annotation { "Feature Type Name" : "Feature", "Feature Type Description" : "" }
export const myFeature = defineFeature(function(context is Context, id is Id, definition is map)
    precondition{}
    {
        {
            var Q0;
            Q0=qCreatedBy(makeId("Top.planeOp"),FACE);
            var sketch = newSketch(context, id + "F0", { "sketchPlane" : qUnion([Q0])});
            skLineSegment(sketch, "E0.bottom", {"start": v(-30.42, 27.45) * mm, "end": v(21.08, 27.45) * mm});
            skLineSegment(sketch, "E0.top", {"start": v(-30.42, -12.55) * mm, "end": v(21.08, -12.55) * mm});
            skLineSegment(sketch, "E0.left", {"start": v(-30.42, 27.45) * mm, "end": v(-30.42, -12.55) * mm});
            skLineSegment(sketch, "E0.right", {"start": v(21.08, 27.45) * mm, "end": v(21.08, -12.55) * mm});
            skLineSegment(sketch, "E1.bottom", {"start": v(-33.42, -15.55) * mm, "end": v(24.08, -15.55) * mm});
            skLineSegment(sketch, "E1.top", {"start": v(-33.42, 30.45) * mm, "end": v(24.08, 30.45) * mm});
            skLineSegment(sketch, "E1.left", {"start": v(-33.42, -15.55) * mm, "end": v(-33.42, 30.45) * mm});
            skLineSegment(sketch, "E1.right", {"start": v(24.08, -15.55) * mm, "end": v(24.08, 30.45) * mm});
            skLineSegment(sketch, "E2.bottom", {"start": v(94.89, 38.7) * mm, "end": v(41.39, 38.7) * mm});
            skLineSegment(sketch, "E2.top", {"start": v(94.89, -4.3) * mm, "end": v(41.39, -4.3) * mm});
            skLineSegment(sketch, "E2.left", {"start": v(94.89, 38.7) * mm, "end": v(94.89, -4.3) * mm});
            skLineSegment(sketch, "E2.right", {"start": v(41.39, 38.7) * mm, "end": v(41.39, -4.3) * mm});
            skSolve(sketch);
        }
        {
            var Q0;
            Q0=makeQuery(id+"F0.imprint","IMPRINT",FACE,{"disambiguationData":[TD([[makeQuery(id+"F0.imprint","IMPRINT",EDGE,{"derivedFrom":sQuery(id+"F0.wireOp",EDGE,"E0.bottom")}),-1.0]])]});
            extrude(context, id + "F1", {"entities" : qUnion([Q0]), "depth" : 31 * mm, "offsetDistance" : 25 * mm});
        }
        {
            var Q0;
            Q0=makeQuery(id+"F1.opExtrude","CAP_FACE",FACE,{"disambiguationData":[OSD([sQuery(id+"F0.wireOp",EDGE,"E0.bottom"),sQuery(id+"F0.wireOp",EDGE,"E0.top"),sQuery(id+"F0.wireOp",EDGE,"E0.left"),sQuery(id+"F0.wireOp",EDGE,"E0.right")])],"isStart":false});
            var sketch = newSketch(context, id + "F2", { "sketchPlane" : qUnion([Q0])});
            skLineSegment(sketch, "E3.bottom", {"start": v(-27.42, 24.45) * mm, "end": v(-24.42, 24.45) * mm});
            skLineSegment(sketch, "E3.top", {"start": v(-27.42, -2.55) * mm, "end": v(-24.42, -2.55) * mm});
            skLineSegment(sketch, "E3.left", {"start": v(-27.42, 24.45) * mm, "end": v(-27.42, -2.55) * mm});
            skLineSegment(sketch, "E3.right", {"start": v(-24.42, 24.45) * mm, "end": v(-24.42, -2.55) * mm});
            skLineSegment(sketch, "E4.bottom", {"start": v(-21.92, 24.45) * mm, "end": v(-18.92, 24.45) * mm});
            skLineSegment(sketch, "E4.top", {"start": v(-21.92, -2.55) * mm, "end": v(-18.92, -2.55) * mm});
            skLineSegment(sketch, "E4.left", {"start": v(-21.92, 24.45) * mm, "end": v(-21.92, -2.55) * mm});
            skLineSegment(sketch, "E4.right", {"start": v(-18.92, 24.45) * mm, "end": v(-18.92, -2.55) * mm});
            skLineSegment(sketch, "E5.bottom", {"start": v(-16.42, 24.45) * mm, "end": v(-13.42, 24.45) * mm});
            skLineSegment(sketch, "E5.top", {"start": v(-16.42, -2.55) * mm, "end": v(-13.42, -2.55) * mm});
            skLineSegment(sketch, "E5.left", {"start": v(-16.42, 24.45) * mm, "end": v(-16.42, -2.55) * mm});
            skLineSegment(sketch, "E5.right", {"start": v(-13.42, 24.45) * mm, "end": v(-13.42, -2.55) * mm});
            skLineSegment(sketch, "E6.bottom", {"start": v(-10.92, 24.45) * mm, "end": v(-7.92, 24.45) * mm});
            skLineSegment(sketch, "E6.top", {"start": v(-10.92, -2.55) * mm, "end": v(-7.92, -2.55) * mm});
            skLineSegment(sketch, "E6.left", {"start": v(-10.92, 24.45) * mm, "end": v(-10.92, -2.55) * mm});
            skLineSegment(sketch, "E6.right", {"start": v(-7.92, 24.45) * mm, "end": v(-7.92, -2.55) * mm});
            skLineSegment(sketch, "E7.bottom", {"start": v(-5.42, 24.45) * mm, "end": v(-2.42, 24.45) * mm});
            skLineSegment(sketch, "E7.top", {"start": v(-5.42, -2.55) * mm, "end": v(-2.42, -2.55) * mm});
            skLineSegment(sketch, "E7.left", {"start": v(-5.42, 24.45) * mm, "end": v(-5.42, -2.55) * mm});
            skLineSegment(sketch, "E7.right", {"start": v(-2.42, 24.45) * mm, "end": v(-2.42, -2.55) * mm});
            skLineSegment(sketch, "E8.bottom", {"start": v(0.08, 24.45) * mm, "end": v(3.08, 24.45) * mm});
            skLineSegment(sketch, "E8.top", {"start": v(0.08, -2.55) * mm, "end": v(3.08, -2.55) * mm});
            skLineSegment(sketch, "E8.left", {"start": v(0.08, 24.45) * mm, "end": v(0.08, -2.55) * mm});
            skLineSegment(sketch, "E8.right", {"start": v(3.08, 24.45) * mm, "end": v(3.08, -2.55) * mm});
            skLineSegment(sketch, "E9.bottom", {"start": v(5.58, 24.45) * mm, "end": v(8.58, 24.45) * mm});
            skLineSegment(sketch, "E9.top", {"start": v(5.58, -2.55) * mm, "end": v(8.58, -2.55) * mm});
            skLineSegment(sketch, "E9.left", {"start": v(5.58, 24.45) * mm, "end": v(5.58, -2.55) * mm});
            skLineSegment(sketch, "E9.right", {"start": v(8.58, 24.45) * mm, "end": v(8.58, -2.55) * mm});
            skLineSegment(sketch, "E10.bottom", {"start": v(11.08, 24.45) * mm, "end": v(14.08, 24.45) * mm});
            skLineSegment(sketch, "E10.top", {"start": v(11.08, -2.55) * mm, "end": v(14.08, -2.55) * mm});
            skLineSegment(sketch, "E10.left", {"start": v(11.08, 24.45) * mm, "end": v(11.08, -2.55) * mm});
            skLineSegment(sketch, "E10.right", {"start": v(14.08, 24.45) * mm, "end": v(14.08, -2.55) * mm});
            skLineSegment(sketch, "E11.bottom", {"start": v(-27.42, -4.55) * mm, "end": v(-14.42, -4.55) * mm});
            skLineSegment(sketch, "E11.top", {"start": v(-27.42, -6.25) * mm, "end": v(-14.42, -6.25) * mm});
            skLineSegment(sketch, "E11.left", {"start": v(-27.42, -4.55) * mm, "end": v(-27.42, -6.25) * mm});
            skLineSegment(sketch, "E11.right", {"start": v(-14.42, -4.55) * mm, "end": v(-14.42, -6.25) * mm});
            skLineSegment(sketch, "E12.bottom", {"start": v(-27.42, -8.25) * mm, "end": v(-14.42, -8.25) * mm});
            skLineSegment(sketch, "E12.top", {"start": v(-27.42, -9.75) * mm, "end": v(-14.42, -9.75) * mm});
            skLineSegment(sketch, "E12.left", {"start": v(-27.42, -8.25) * mm, "end": v(-27.42, -9.75) * mm});
            skLineSegment(sketch, "E12.right", {"start": v(-14.42, -8.25) * mm, "end": v(-14.42, -9.75) * mm});
            skLineSegment(sketch, "E13.bottom", {"start": v(-12.92, -4.55) * mm, "end": v(0.08, -4.55) * mm});
            skLineSegment(sketch, "E13.top", {"start": v(-12.92, -6.25) * mm, "end": v(0.08, -6.25) * mm});
            skLineSegment(sketch, "E13.left", {"start": v(-12.92, -4.55) * mm, "end": v(-12.92, -6.25) * mm});
            skLineSegment(sketch, "E13.right", {"start": v(0.08, -4.55) * mm, "end": v(0.08, -6.25) * mm});
            skLineSegment(sketch, "E14.bottom", {"start": v(-12.92, -8.25) * mm, "end": v(0.08, -8.25) * mm});
            skLineSegment(sketch, "E14.top", {"start": v(-12.92, -9.75) * mm, "end": v(0.08, -9.75) * mm});
            skLineSegment(sketch, "E14.left", {"start": v(-12.92, -8.25) * mm, "end": v(-12.92, -9.75) * mm});
            skLineSegment(sketch, "E14.right", {"start": v(0.08, -8.25) * mm, "end": v(0.08, -9.75) * mm});
            skLineSegment(sketch, "E15.bottom", {"start": v(1.58, -4.55) * mm, "end": v(14.58, -4.55) * mm});
            skLineSegment(sketch, "E15.top", {"start": v(1.58, -6.25) * mm, "end": v(14.58, -6.25) * mm});
            skLineSegment(sketch, "E15.left", {"start": v(1.58, -4.55) * mm, "end": v(1.58, -6.25) * mm});
            skLineSegment(sketch, "E15.right", {"start": v(14.58, -4.55) * mm, "end": v(14.58, -6.25) * mm});
            skLineSegment(sketch, "E16.bottom", {"start": v(1.58, -8.25) * mm, "end": v(14.58, -8.25) * mm});
            skLineSegment(sketch, "E16.top", {"start": v(1.58, -9.75) * mm, "end": v(14.58, -9.75) * mm});
            skLineSegment(sketch, "E16.left", {"start": v(1.58, -8.25) * mm, "end": v(1.58, -9.75) * mm});
            skLineSegment(sketch, "E16.right", {"start": v(14.58, -8.25) * mm, "end": v(14.58, -9.75) * mm});
            skLineSegment(sketch, "E17.bottom", {"start": v(16.58, -2.55) * mm, "end": v(18.08, -2.55) * mm});
            skLineSegment(sketch, "E17.top", {"start": v(16.58, 9.95) * mm, "end": v(18.08, 9.95) * mm});
            skLineSegment(sketch, "E17.left", {"start": v(16.58, -2.55) * mm, "end": v(16.58, 9.95) * mm});
            skLineSegment(sketch, "E17.right", {"start": v(18.08, -2.55) * mm, "end": v(18.08, 9.95) * mm});
            skLineSegment(sketch, "E18.bottom", {"start": v(18.08, 11.95) * mm, "end": v(16.58, 11.95) * mm});
            skLineSegment(sketch, "E18.top", {"start": v(18.08, 24.45) * mm, "end": v(16.58, 24.45) * mm});
            skLineSegment(sketch, "E18.left", {"start": v(18.08, 11.95) * mm, "end": v(18.08, 24.45) * mm});
            skLineSegment(sketch, "E18.right", {"start": v(16.58, 11.95) * mm, "end": v(16.58, 24.45) * mm});
            skSolve(sketch);
        }
        {
            var Q0;
            Q0=makeQuery(id+"F2.imprint","IMPRINT",FACE,{"disambiguationData":[TD([[makeQuery(id+"F2.imprint","IMPRINT",EDGE,{"derivedFrom":sQuery(id+"F2.wireOp",EDGE,"E3.bottom")}),-1.0]])]});
            var Q1;
            Q1=makeQuery(id+"F2.imprint","IMPRINT",FACE,{"disambiguationData":[TD([[makeQuery(id+"F2.imprint","IMPRINT",EDGE,{"derivedFrom":sQuery(id+"F2.wireOp",EDGE,"E4.bottom")}),-1.0]])]});
            var Q2;
            Q2=makeQuery(id+"F2.imprint","IMPRINT",FACE,{"disambiguationData":[TD([[makeQuery(id+"F2.imprint","IMPRINT",EDGE,{"derivedFrom":sQuery(id+"F2.wireOp",EDGE,"E5.bottom")}),-1.0]])]});
            var Q3;
            Q3=makeQuery(id+"F2.imprint","IMPRINT",FACE,{"disambiguationData":[TD([[makeQuery(id+"F2.imprint","IMPRINT",EDGE,{"derivedFrom":sQuery(id+"F2.wireOp",EDGE,"E6.bottom")}),-1.0]])]});
            var Q4;
            Q4=makeQuery(id+"F2.imprint","IMPRINT",FACE,{"disambiguationData":[TD([[makeQuery(id+"F2.imprint","IMPRINT",EDGE,{"derivedFrom":sQuery(id+"F2.wireOp",EDGE,"E7.bottom")}),-1.0]])]});
            var Q5;
            Q5=makeQuery(id+"F2.imprint","IMPRINT",FACE,{"disambiguationData":[TD([[makeQuery(id+"F2.imprint","IMPRINT",EDGE,{"derivedFrom":sQuery(id+"F2.wireOp",EDGE,"E8.bottom")}),-1.0]])]});
            var Q6;
            Q6=makeQuery(id+"F2.imprint","IMPRINT",FACE,{"disambiguationData":[TD([[makeQuery(id+"F2.imprint","IMPRINT",EDGE,{"derivedFrom":sQuery(id+"F2.wireOp",EDGE,"E9.bottom")}),-1.0]])]});
            var Q7;
            Q7=makeQuery(id+"F2.imprint","IMPRINT",FACE,{"disambiguationData":[TD([[makeQuery(id+"F2.imprint","IMPRINT",EDGE,{"derivedFrom":sQuery(id+"F2.wireOp",EDGE,"E10.bottom")}),-1.0]])]});
            extrude(context, id + "F3", {"entities" : qUnion([Q0, Q1, Q2, Q3, Q4, Q5, Q6, Q7]), "operationType" : NewBodyOperationType.REMOVE, "oppositeDirection" : true, "depth" : 28 * mm, "offsetDistance" : 25 * mm});
        }
        {
            var Q0;
            Q0=makeQuery(id+"F2.imprint","IMPRINT",FACE,{"disambiguationData":[TD([[makeQuery(id+"F2.imprint","IMPRINT",EDGE,{"derivedFrom":sQuery(id+"F2.wireOp",EDGE,"E11.bottom")}),-1.0]])]});
            var Q1;
            Q1=makeQuery(id+"F2.imprint","IMPRINT",FACE,{"disambiguationData":[TD([[makeQuery(id+"F2.imprint","IMPRINT",EDGE,{"derivedFrom":sQuery(id+"F2.wireOp",EDGE,"E13.bottom")}),-1.0]])]});
            var Q2;
            Q2=makeQuery(id+"F2.imprint","IMPRINT",FACE,{"disambiguationData":[TD([[makeQuery(id+"F2.imprint","IMPRINT",EDGE,{"derivedFrom":sQuery(id+"F2.wireOp",EDGE,"E15.bottom")}),-1.0]])]});
            var Q3;
            Q3=makeQuery(id+"F2.imprint","IMPRINT",FACE,{"disambiguationData":[TD([[makeQuery(id+"F2.imprint","IMPRINT",EDGE,{"derivedFrom":sQuery(id+"F2.wireOp",EDGE,"E16.bottom")}),-1.0]])]});
            var Q4;
            Q4=makeQuery(id+"F2.imprint","IMPRINT",FACE,{"disambiguationData":[TD([[makeQuery(id+"F2.imprint","IMPRINT",EDGE,{"derivedFrom":sQuery(id+"F2.wireOp",EDGE,"E14.bottom")}),-1.0]])]});
            var Q5;
            Q5=makeQuery(id+"F2.imprint","IMPRINT",FACE,{"disambiguationData":[TD([[makeQuery(id+"F2.imprint","IMPRINT",EDGE,{"derivedFrom":sQuery(id+"F2.wireOp",EDGE,"E12.bottom")}),-1.0]])]});
            var Q6;
            Q6=makeQuery(id+"F2.imprint","IMPRINT",FACE,{"disambiguationData":[TD([[makeQuery(id+"F2.imprint","IMPRINT",EDGE,{"derivedFrom":sQuery(id+"F2.wireOp",EDGE,"E17.bottom")}),1.0]])]});
            var Q7;
            Q7=makeQuery(id+"F2.imprint","IMPRINT",FACE,{"disambiguationData":[TD([[makeQuery(id+"F2.imprint","IMPRINT",EDGE,{"derivedFrom":sQuery(id+"F2.wireOp",EDGE,"E18.bottom")}),-1.0]])]});
            extrude(context, id + "F4", {"entities" : qUnion([Q0, Q1, Q2, Q3, Q4, Q5, Q6, Q7]), "operationType" : NewBodyOperationType.REMOVE, "oppositeDirection" : true, "depth" : 11 * mm, "offsetDistance" : 25 * mm});
        }
        {
            var Q0;
            Q0=makeQuery(id+"F0.imprint","IMPRINT",FACE,{"disambiguationData":[TD([[makeQuery(id+"F0.imprint","IMPRINT",EDGE,{"derivedFrom":sQuery(id+"F0.wireOp",EDGE,"E0.bottom")}),1.0]])]});
            extrude(context, id + "F5", {"entities" : qUnion([Q0]), "operationType" : NewBodyOperationType.ADD, "depth" : 20 * mm, "offsetDistance" : 25 * mm});
        }
        {
            var Q0;
            Q0=makeQuery(id+"F0.imprint","IMPRINT",FACE,{"disambiguationData":[TD([[makeQuery(id+"F0.imprint","IMPRINT",EDGE,{"derivedFrom":sQuery(id+"F0.wireOp",EDGE,"E2.bottom")}),1.0]])]});
            extrude(context, id + "F6", {"entities" : qUnion([Q0]), "depth" : 20 * mm, "offsetDistance" : 25 * mm});
        }
        {
            var Q0;
            Q0=makeQuery(id+"F6.opExtrude","CAP_FACE",FACE,{"disambiguationData":[OSD([sQuery(id+"F0.wireOp",EDGE,"E2.bottom"),sQuery(id+"F0.wireOp",EDGE,"E2.top"),sQuery(id+"F0.wireOp",EDGE,"E2.left"),sQuery(id+"F0.wireOp",EDGE,"E2.right")])],"isStart":false});
            var sketch = newSketch(context, id + "F7", { "sketchPlane" : qUnion([Q0])});
            skLineSegment(sketch, "E19.bottom", {"start": v(44.29, 35.8) * mm, "end": v(91.99, 35.8) * mm});
            skLineSegment(sketch, "E19.top", {"start": v(44.29, -1.4) * mm, "end": v(91.99, -1.4) * mm});
            skLineSegment(sketch, "E19.left", {"start": v(44.29, 35.8) * mm, "end": v(44.29, -1.4) * mm});
            skLineSegment(sketch, "E19.right", {"start": v(91.99, 35.8) * mm, "end": v(91.99, -1.4) * mm});
            skSolve(sketch);
        }
        {
            var Q0;
            Q0=makeQuery(id+"F7.imprint","IMPRINT",FACE,{"disambiguationData":[TD([[makeQuery(id+"F7.imprint","IMPRINT",EDGE,{"derivedFrom":sQuery(id+"F7.wireOp",EDGE,"E19.bottom")}),-1.0]])]});
            extrude(context, id + "F8", {"entities" : qUnion([Q0]), "operationType" : NewBodyOperationType.REMOVE, "oppositeDirection" : true, "depth" : 17 * mm, "offsetDistance" : 25 * mm});
        }
        {
            var Q0;
            Q0=makeQuery(id+"F8.boolean.opBoolean","COPY",FACE,{"derivedFrom":makeQuery(id+"F8.opExtrude","CAP_FACE",FACE,{"disambiguationData":[OSD([sQuery(id+"F7.wireOp",EDGE,"E19.bottom"),sQuery(id+"F7.wireOp",EDGE,"E19.top"),sQuery(id+"F7.wireOp",EDGE,"E19.left"),sQuery(id+"F7.wireOp",EDGE,"E19.right")])],"isStart":false})});
            fillet(context, id + "F9", {"entities" : qUnion([Q0]), "radius" : 2.5 * mm, "tangentPropagation" : true, "allowEdgeOverflow" : false});
        }
        {
            var Q0;
            Q0=makeQuery(id+"F1.opExtrude","SWEPT_EDGE",EDGE,{"disambiguationData":[OSD([sQuery(id+"F0.wireOp",EDGE,"E0.bottom"),sQuery(id+"F0.wireOp",EDGE,"E0.right")])]});
            var Q1;
            Q1=makeQuery(id+"F1.opExtrude","SWEPT_EDGE",EDGE,{"disambiguationData":[OSD([sQuery(id+"F0.wireOp",EDGE,"E0.bottom"),sQuery(id+"F0.wireOp",EDGE,"E0.left")])]});
            var Q2;
            Q2=makeQuery(id+"F1.opExtrude","SWEPT_EDGE",EDGE,{"disambiguationData":[OSD([sQuery(id+"F0.wireOp",EDGE,"E0.top"),sQuery(id+"F0.wireOp",EDGE,"E0.right")])]});
            var Q3;
            Q3=makeQuery(id+"F1.opExtrude","SWEPT_EDGE",EDGE,{"disambiguationData":[OSD([sQuery(id+"F0.wireOp",EDGE,"E0.top"),sQuery(id+"F0.wireOp",EDGE,"E0.left")])]});
            fillet(context, id + "F10", {"entities" : qUnion([Q0, Q1, Q2, Q3]), "radius" : 3 * mm, "tangentPropagation" : true, "allowEdgeOverflow" : false});
        }
        {
            var Q0;
            {var subQ0=sQuery(id+"F0.wireOp",EDGE,"E0.right");var subQ1=sQuery(id+"F0.wireOp",EDGE,"E0.left");var subQ2=sQuery(id+"F0.wireOp",EDGE,"E0.top");var subQ3=sQuery(id+"F0.wireOp",EDGE,"E0.bottom");Q0=makeQuery(id+"F5.boolean.opBoolean","MERGE",FACE,{"derivedFrom":[makeQuery(id+"F1.opExtrude","CAP_FACE",FACE,{"disambiguationData":[OSD([subQ3,subQ2,subQ1,subQ0])],"isStart":true}),makeQuery(id+"F5.opExtrude","CAP_FACE",FACE,{"disambiguationData":[OSD([subQ3,subQ2,subQ1,subQ0,sQuery(id+"F0.wireOp",EDGE,"E1.bottom"),sQuery(id+"F0.wireOp",EDGE,"E1.top"),sQuery(id+"F0.wireOp",EDGE,"E1.left"),sQuery(id+"F0.wireOp",EDGE,"E1.right")])],"isStart":true})]});}
            fillet(context, id + "F11", {"entities" : qUnion([Q0]), "radius" : 1.5 * mm, "tangentPropagation" : true, "allowEdgeOverflow" : false});
        }
        {
            var Q0;
            Q0=makeQuery(id+"F6.opExtrude","SWEPT_EDGE",EDGE,{"disambiguationData":[OSD([sQuery(id+"F0.wireOp",EDGE,"E2.bottom"),sQuery(id+"F0.wireOp",EDGE,"E2.left")])]});
            var Q1;
            Q1=makeQuery(id+"F6.opExtrude","SWEPT_EDGE",EDGE,{"disambiguationData":[OSD([sQuery(id+"F0.wireOp",EDGE,"E2.bottom"),sQuery(id+"F0.wireOp",EDGE,"E2.right")])]});
            var Q2;
            Q2=makeQuery(id+"F6.opExtrude","SWEPT_EDGE",EDGE,{"disambiguationData":[OSD([sQuery(id+"F0.wireOp",EDGE,"E2.top"),sQuery(id+"F0.wireOp",EDGE,"E2.right")])]});
            var Q3;
            Q3=makeQuery(id+"F6.opExtrude","SWEPT_EDGE",EDGE,{"disambiguationData":[OSD([sQuery(id+"F0.wireOp",EDGE,"E2.top"),sQuery(id+"F0.wireOp",EDGE,"E2.left")])]});
            var Q4;
            Q4=makeQuery(id+"F6.opExtrude","CAP_FACE",FACE,{"disambiguationData":[OSD([sQuery(id+"F0.wireOp",EDGE,"E2.bottom"),sQuery(id+"F0.wireOp",EDGE,"E2.top"),sQuery(id+"F0.wireOp",EDGE,"E2.left"),sQuery(id+"F0.wireOp",EDGE,"E2.right")])],"isStart":true});
            fillet(context, id + "F12", {"entities" : qUnion([Q0, Q1, Q2, Q3, Q4]), "radius" : 3 * mm, "tangentPropagation" : true, "allowEdgeOverflow" : false});
        }
        {
            var Q0;
            Q0=makeQuery(id+"F8.boolean.opBoolean","COPY",EDGE,{"derivedFrom":makeQuery(id+"F8.opExtrude","CAP_EDGE",EDGE,{"disambiguationData":[OSD([sQuery(id+"F7.wireOp",EDGE,"E19.top")])],"isStart":true})});
            var Q1;
            Q1=makeQuery(id+"F8.boolean.opBoolean","COPY",EDGE,{"derivedFrom":makeQuery(id+"F8.opExtrude","CAP_EDGE",EDGE,{"disambiguationData":[OSD([sQuery(id+"F7.wireOp",EDGE,"E19.right")])],"isStart":true})});
            var Q2;
            Q2=makeQuery(id+"F8.boolean.opBoolean","COPY",EDGE,{"derivedFrom":makeQuery(id+"F8.opExtrude","CAP_EDGE",EDGE,{"disambiguationData":[OSD([sQuery(id+"F7.wireOp",EDGE,"E19.bottom")])],"isStart":true})});
            var Q3;
            Q3=makeQuery(id+"F8.boolean.opBoolean","COPY",EDGE,{"derivedFrom":makeQuery(id+"F8.opExtrude","CAP_EDGE",EDGE,{"disambiguationData":[OSD([sQuery(id+"F7.wireOp",EDGE,"E19.left")])],"isStart":true})});
            var Q4;
            Q4=makeQuery(id+"F8.boolean.opBoolean","COPY",EDGE,{"derivedFrom":makeQuery(id+"F8.opExtrude","SWEPT_EDGE",EDGE,{"disambiguationData":[OSD([sQuery(id+"F7.wireOp",EDGE,"E19.top"),sQuery(id+"F7.wireOp",EDGE,"E19.left")])]})});
            var Q5;
            Q5=makeQuery(id+"F8.boolean.opBoolean","COPY",EDGE,{"derivedFrom":makeQuery(id+"F8.opExtrude","SWEPT_EDGE",EDGE,{"disambiguationData":[OSD([sQuery(id+"F7.wireOp",EDGE,"E19.bottom"),sQuery(id+"F7.wireOp",EDGE,"E19.left")])]})});
            var Q6;
            Q6=makeQuery(id+"F8.boolean.opBoolean","COPY",EDGE,{"derivedFrom":makeQuery(id+"F8.opExtrude","SWEPT_EDGE",EDGE,{"disambiguationData":[OSD([sQuery(id+"F7.wireOp",EDGE,"E19.bottom"),sQuery(id+"F7.wireOp",EDGE,"E19.right")])]})});
            var Q7;
            Q7=makeQuery(id+"F8.boolean.opBoolean","COPY",EDGE,{"derivedFrom":makeQuery(id+"F8.opExtrude","SWEPT_EDGE",EDGE,{"disambiguationData":[OSD([sQuery(id+"F7.wireOp",EDGE,"E19.top"),sQuery(id+"F7.wireOp",EDGE,"E19.right")])]})});
            fillet(context, id + "F13", {"entities" : qUnion([Q0, Q1, Q2, Q3, Q4, Q5, Q6, Q7]), "radius" : 1 * mm, "tangentPropagation" : true, "allowEdgeOverflow" : false});
        }
        {
            var Q0;
            Q0=makeQuery(id+"F1.opExtrude","CAP_EDGE",EDGE,{"disambiguationData":[OSD([sQuery(id+"F0.wireOp",EDGE,"E0.bottom")])],"isStart":false});
            fillet(context, id + "F14", {"entities" : qUnion([Q0]), "radius" : 1 * mm, "tangentPropagation" : true, "allowEdgeOverflow" : false});
        }
        {
            var Q0;
            Q0=makeQuery(id+"F5.opExtrude","SWEPT_EDGE",EDGE,{"disambiguationData":[OSD([sQuery(id+"F0.wireOp",EDGE,"E1.top"),sQuery(id+"F0.wireOp",EDGE,"E1.right")])]});
            var Q1;
            Q1=makeQuery(id+"F5.opExtrude","SWEPT_EDGE",EDGE,{"disambiguationData":[OSD([sQuery(id+"F0.wireOp",EDGE,"E1.top"),sQuery(id+"F0.wireOp",EDGE,"E1.left")])]});
            var Q2;
            Q2=makeQuery(id+"F5.opExtrude","SWEPT_EDGE",EDGE,{"disambiguationData":[OSD([sQuery(id+"F0.wireOp",EDGE,"E1.bottom"),sQuery(id+"F0.wireOp",EDGE,"E1.left")])]});
            var Q3;
            Q3=makeQuery(id+"F5.opExtrude","SWEPT_EDGE",EDGE,{"disambiguationData":[OSD([sQuery(id+"F0.wireOp",EDGE,"E1.bottom"),sQuery(id+"F0.wireOp",EDGE,"E1.right")])]});
            fillet(context, id + "F15", {"entities" : qUnion([Q0, Q1, Q2, Q3]), "radius" : 3 * mm, "tangentPropagation" : true, "allowEdgeOverflow" : false});
        }
        {
            var Q0;
            Q0=makeQuery(id+"F8.boolean.opBoolean","COPY",FACE,{"derivedFrom":makeQuery(id+"F8.opExtrude","CAP_FACE",FACE,{"disambiguationData":[OSD([sQuery(id+"F7.wireOp",EDGE,"E19.bottom"),sQuery(id+"F7.wireOp",EDGE,"E19.top"),sQuery(id+"F7.wireOp",EDGE,"E19.left"),sQuery(id+"F7.wireOp",EDGE,"E19.right")])],"isStart":false})});
            var sketch = newSketch(context, id + "F16", { "sketchPlane" : qUnion([Q0])});
            skText(sketch, "E20", { "text": "RORY PARKYN", "fontName": "RobotoSlab-Bold.ttf"});
            skText(sketch, "E21", { "text": "0211299177", "fontName": "RobotoSlab-Bold.ttf"});
            skLineSegment(sketch, "E22", {"start": v(61.25, 30.07) * mm, "end": v(62.9, 18.88) * mm});
            skLineSegment(sketch, "E23", {"start": v(62.9, 18.88) * mm, "end": v(73.8, 20.49) * mm});
            skLineSegment(sketch, "E24", {"start": v(72.19, 31.68) * mm, "end": v(61.25, 30.07) * mm});
            skLineSegment(sketch, "E25", {"start": v(62.23, 23.46) * mm, "end": v(65.58, 30.7) * mm});
            skLineSegment(sketch, "E26", {"start": v(67.37, 30.97) * mm, "end": v(63.31, 22.25) * mm});
            skLineSegment(sketch, "E27", {"start": v(63.31, 22.25) * mm, "end": v(64.5, 21.7) * mm});
            skLineSegment(sketch, "E28", {"start": v(64.5, 21.7) * mm, "end": v(65.13, 23.05) * mm});
            skLineSegment(sketch, "E29", {"start": v(65.13, 23.05) * mm, "end": v(66.51, 22.4) * mm});
            skLineSegment(sketch, "E30", {"start": v(66.51, 22.4) * mm, "end": v(65.87, 21.02) * mm});
            skLineSegment(sketch, "E31", {"start": v(65.87, 21.02) * mm, "end": v(67.1, 20.45) * mm});
            skLineSegment(sketch, "E32", {"start": v(67.1, 20.45) * mm, "end": v(68.24, 22.9) * mm});
            skLineSegment(sketch, "E33", {"start": v(68.24, 22.9) * mm, "end": v(65.63, 24.1) * mm});
            skLineSegment(sketch, "E34", {"start": v(65.63, 24.1) * mm, "end": v(66.27, 25.46) * mm});
            skLineSegment(sketch, "E35", {"start": v(66.27, 25.46) * mm, "end": v(68.81, 24.28) * mm});
            skLineSegment(sketch, "E36", {"start": v(68.81, 24.28) * mm, "end": v(69.37, 25.47) * mm});
            skLineSegment(sketch, "E37", {"start": v(69.37, 25.47) * mm, "end": v(66.8, 26.66) * mm});
            skLineSegment(sketch, "E38", {"start": v(66.8, 26.66) * mm, "end": v(67.44, 28.03) * mm});
            skLineSegment(sketch, "E39", {"start": v(67.44, 28.03) * mm, "end": v(69.96, 26.85) * mm});
            skLineSegment(sketch, "E40", {"start": v(69.96, 26.85) * mm, "end": v(70.56, 28.15) * mm});
            skLineSegment(sketch, "E41", {"start": v(70.56, 28.15) * mm, "end": v(68.04, 29.32) * mm});
            skLineSegment(sketch, "E42", {"start": v(68.04, 29.32) * mm, "end": v(68.66, 30.66) * mm});
            skLineSegment(sketch, "E43", {"start": v(68.66, 30.66) * mm, "end": v(72.6, 28.83) * mm});
            skLineSegment(sketch, "E44", {"start": v(72.6, 28.83) * mm, "end": v(68.4, 19.7) * mm});
            skLineSegment(sketch, "E45", {"start": v(62.61, 20.81) * mm, "end": v(65.8, 19.31) * mm});
            skLineSegment(sketch, "E46.bottom", {"start": v(58.85, 32.31) * mm, "end": v(76.96, 32.31) * mm});
            skLineSegment(sketch, "E46.top", {"start": v(58.85, 17.78) * mm, "end": v(76.96, 17.78) * mm});
            skLineSegment(sketch, "E46.left", {"start": v(58.85, 32.31) * mm, "end": v(58.85, 17.78) * mm});
            skLineSegment(sketch, "E46.right", {"start": v(76.96, 32.31) * mm, "end": v(76.96, 17.78) * mm});
            skLineSegment(sketch, "E47", {"start": v(72.19, 31.68) * mm, "end": v(72.21, 31.68) * mm});
            skLineSegment(sketch, "E48", {"start": v(72.21, 31.68) * mm, "end": v(73.82, 20.5) * mm});
            skLineSegment(sketch, "E49", {"start": v(73.82, 20.5) * mm, "end": v(73.8, 20.49) * mm});
            const initialGuessF16  = {"E20": [0.05284, 0.01355, 1, 0, 0.00301], "E21": [0.0552, 0.0056, 1, 0, 0.00351]};
            skSetInitialGuess(sketch, initialGuessF16);
            skSolve(sketch);
        }
        {
            var Q0;
            Q0=makeQuery(id+"F16.imprint","IMPRINT",FACE,{"disambiguationData":[TD([[makeQuery(id+"F16.imprint","IMPRINT",EDGE,{"derivedFrom":sQuery(id+"F16.wireOp",EDGE,"E20.sketch_text.stroke-92")}),-1.0]])]});
            var Q1;
            Q1=makeQuery(id+"F16.imprint","IMPRINT",FACE,{"disambiguationData":[TD([[makeQuery(id+"F16.imprint","IMPRINT",EDGE,{"derivedFrom":sQuery(id+"F16.wireOp",EDGE,"E20.sketch_text.stroke-193")}),-1.0]])]});
            var Q2;
            Q2=makeQuery(id+"F16.imprint","IMPRINT",FACE,{"disambiguationData":[TD([[makeQuery(id+"F16.imprint","IMPRINT",EDGE,{"derivedFrom":sQuery(id+"F16.wireOp",EDGE,"E20.sketch_text.stroke-222")}),-1.0]])]});
            var Q3;
            Q3=makeQuery(id+"F16.imprint","IMPRINT",FACE,{"disambiguationData":[TD([[makeQuery(id+"F16.imprint","IMPRINT",EDGE,{"derivedFrom":sQuery(id+"F16.wireOp",EDGE,"E20.sketch_text.stroke-244")}),-1.0]])]});
            var Q4;
            Q4=makeQuery(id+"F16.imprint","IMPRINT",FACE,{"disambiguationData":[TD([[makeQuery(id+"F16.imprint","IMPRINT",EDGE,{"derivedFrom":sQuery(id+"F16.wireOp",EDGE,"E21.sketch_text.stroke-20")}),-1.0]])]});
            var Q5;
            Q5=makeQuery(id+"F16.imprint","IMPRINT",FACE,{"disambiguationData":[TD([[makeQuery(id+"F16.imprint","IMPRINT",EDGE,{"derivedFrom":sQuery(id+"F16.wireOp",EDGE,"E21.sketch_text.stroke-43")}),-1.0]])]});
            var Q6;
            Q6=makeQuery(id+"F16.imprint","IMPRINT",FACE,{"disambiguationData":[TD([[makeQuery(id+"F16.imprint","IMPRINT",EDGE,{"derivedFrom":sQuery(id+"F16.wireOp",EDGE,"E21.sketch_text.stroke-53")}),-1.0]])]});
            var Q7;
            Q7=makeQuery(id+"F16.imprint","IMPRINT",FACE,{"disambiguationData":[TD([[makeQuery(id+"F16.imprint","IMPRINT",EDGE,{"derivedFrom":sQuery(id+"F16.wireOp",EDGE,"E21.sketch_text.stroke-63")}),-1.0]])]});
            var Q8;
            Q8=makeQuery(id+"F16.imprint","IMPRINT",FACE,{"disambiguationData":[TD([[makeQuery(id+"F16.imprint","IMPRINT",EDGE,{"derivedFrom":sQuery(id+"F16.wireOp",EDGE,"E21.sketch_text.stroke-142")}),-1.0]])]});
            var Q9;
            Q9=makeQuery(id+"F16.imprint","IMPRINT",FACE,{"disambiguationData":[TD([[makeQuery(id+"F16.imprint","IMPRINT",EDGE,{"derivedFrom":sQuery(id+"F16.wireOp",EDGE,"E21.sketch_text.stroke-152")}),-1.0]])]});
            var Q10;
            Q10=makeQuery(id+"F16.imprint","IMPRINT",FACE,{"disambiguationData":[TD([[makeQuery(id+"F16.imprint","IMPRINT",EDGE,{"derivedFrom":sQuery(id+"F16.wireOp",EDGE,"E21.sketch_text.stroke-165")}),-1.0]])]});
            var Q11;
            Q11=makeQuery(id+"F16.imprint","IMPRINT",FACE,{"disambiguationData":[TD([[makeQuery(id+"F16.imprint","IMPRINT",EDGE,{"derivedFrom":sQuery(id+"F16.wireOp",EDGE,"E20.sketch_text.stroke-0")}),-1.0]])]});
            var Q12;
            Q12=makeQuery(id+"F16.imprint","IMPRINT",FACE,{"disambiguationData":[TD([[makeQuery(id+"F16.imprint","IMPRINT",EDGE,{"derivedFrom":sQuery(id+"F16.wireOp",EDGE,"E20.sketch_text.stroke-36")}),-1.0]])]});
            var Q13;
            Q13=makeQuery(id+"F16.imprint","IMPRINT",FACE,{"disambiguationData":[TD([[makeQuery(id+"F16.imprint","IMPRINT",EDGE,{"derivedFrom":sQuery(id+"F16.wireOp",EDGE,"E20.sketch_text.stroke-56")}),-1.0]])]});
            var Q14;
            Q14=makeQuery(id+"F16.imprint","IMPRINT",FACE,{"disambiguationData":[TD([[makeQuery(id+"F16.imprint","IMPRINT",EDGE,{"derivedFrom":sQuery(id+"F16.wireOp",EDGE,"E20.sketch_text.stroke-114")}),-1.0]])]});
            var Q15;
            Q15=makeQuery(id+"F16.imprint","IMPRINT",FACE,{"disambiguationData":[TD([[makeQuery(id+"F16.imprint","IMPRINT",EDGE,{"derivedFrom":sQuery(id+"F16.wireOp",EDGE,"E20.sketch_text.stroke-137")}),-1.0]])]});
            var Q16;
            Q16=makeQuery(id+"F16.imprint","IMPRINT",FACE,{"disambiguationData":[TD([[makeQuery(id+"F16.imprint","IMPRINT",EDGE,{"derivedFrom":sQuery(id+"F16.wireOp",EDGE,"E20.sketch_text.stroke-157")}),-1.0]])]});
            var Q17;
            Q17=makeQuery(id+"F16.imprint","IMPRINT",FACE,{"disambiguationData":[TD([[makeQuery(id+"F16.imprint","IMPRINT",EDGE,{"derivedFrom":sQuery(id+"F16.wireOp",EDGE,"E21.sketch_text.stroke-0")}),-1.0]])]});
            var Q18;
            Q18=makeQuery(id+"F16.imprint","IMPRINT",FACE,{"disambiguationData":[TD([[makeQuery(id+"F16.imprint","IMPRINT",EDGE,{"derivedFrom":sQuery(id+"F16.wireOp",EDGE,"E21.sketch_text.stroke-86")}),-1.0]])]});
            var Q19;
            Q19=makeQuery(id+"F16.imprint","IMPRINT",FACE,{"disambiguationData":[TD([[makeQuery(id+"F16.imprint","IMPRINT",EDGE,{"derivedFrom":sQuery(id+"F16.wireOp",EDGE,"E21.sketch_text.stroke-114")}),-1.0]])]});
            var Q20;
            {var subQ0=sQuery(id+"F16.wireOp",EDGE,"E25");Q20=makeQuery(id+"F16.imprint","IMPRINT",FACE,{"disambiguationData":[TD([[makeQuery(id+"F16.imprint","IMPRINT",EDGE,{"derivedFrom":subQ0}),-1.0]])]});}
            extrude(context, id + "F17", {"entities" : qUnion([Q0, Q1, Q2, Q3, Q4, Q5, Q6, Q7, Q8, Q9, Q10, Q11, Q12, Q13, Q14, Q15, Q16, Q17, Q18, Q19, Q20]), "operationType" : NewBodyOperationType.REMOVE, "oppositeDirection" : true, "depth" : 1.5 * mm, "offsetDistance" : 25 * mm});
        }
        {
            var Q0;
            Q0=makeQuery(id+"F16.imprint","IMPRINT",FACE,{"disambiguationData":[TD([[makeQuery(id+"F16.imprint","IMPRINT",EDGE,{"derivedFrom":sQuery(id+"F16.wireOp",EDGE,"E46.bottom")}),-1.0]])]});
            var Q1;
            {var subQ0=sQuery(id+"F16.wireOp",EDGE,"E25");Q1=makeQuery(id+"F16.imprint","IMPRINT",FACE,{"disambiguationData":[TD([[makeQuery(id+"F16.imprint","IMPRINT",EDGE,{"derivedFrom":subQ0}),-1.0]])]});}
            extrude(context, id + "F18", {"entities" : qUnion([Q0, Q1]), "operationType" : NewBodyOperationType.REMOVE, "oppositeDirection" : true, "depth" : 1.5 * mm, "offsetDistance" : 25 * mm});
        }
        {
            var Q0;
            Q0=makeQuery(id+"F17.boolean.opBoolean","COPY",EDGE,{"derivedFrom":makeQuery(id+"F17.opExtrude","SWEPT_EDGE",EDGE,{"disambiguationData":[OSD([sQuery(id+"F16.wireOp",EDGE,"E28"),sQuery(id+"F16.wireOp",EDGE,"E29")])]})});
            var Q1;
            Q1=makeQuery(id+"F17.boolean.opBoolean","COPY",EDGE,{"derivedFrom":makeQuery(id+"F17.opExtrude","SWEPT_EDGE",EDGE,{"disambiguationData":[OSD([sQuery(id+"F16.wireOp",EDGE,"E29"),sQuery(id+"F16.wireOp",EDGE,"E30")])]})});
            var Q2;
            Q2=makeQuery(id+"F17.boolean.opBoolean","COPY",EDGE,{"derivedFrom":makeQuery(id+"F17.opExtrude","SWEPT_EDGE",EDGE,{"disambiguationData":[OSD([sQuery(id+"F16.wireOp",EDGE,"E33"),sQuery(id+"F16.wireOp",EDGE,"E34")])]})});
            var Q3;
            Q3=makeQuery(id+"F17.boolean.opBoolean","COPY",EDGE,{"derivedFrom":makeQuery(id+"F17.opExtrude","SWEPT_EDGE",EDGE,{"disambiguationData":[OSD([sQuery(id+"F16.wireOp",EDGE,"E34"),sQuery(id+"F16.wireOp",EDGE,"E35")])]})});
            var Q4;
            Q4=makeQuery(id+"F17.boolean.opBoolean","COPY",EDGE,{"derivedFrom":makeQuery(id+"F17.opExtrude","SWEPT_EDGE",EDGE,{"disambiguationData":[OSD([sQuery(id+"F16.wireOp",EDGE,"E37"),sQuery(id+"F16.wireOp",EDGE,"E38")])]})});
            var Q5;
            Q5=makeQuery(id+"F17.boolean.opBoolean","COPY",EDGE,{"derivedFrom":makeQuery(id+"F17.opExtrude","SWEPT_EDGE",EDGE,{"disambiguationData":[OSD([sQuery(id+"F16.wireOp",EDGE,"E38"),sQuery(id+"F16.wireOp",EDGE,"E39")])]})});
            var Q6;
            Q6=makeQuery(id+"F17.boolean.opBoolean","COPY",EDGE,{"derivedFrom":makeQuery(id+"F17.opExtrude","SWEPT_EDGE",EDGE,{"disambiguationData":[OSD([sQuery(id+"F16.wireOp",EDGE,"E41"),sQuery(id+"F16.wireOp",EDGE,"E42")])]})});
            var Q7;
            Q7=makeQuery(id+"F17.boolean.opBoolean","COPY",EDGE,{"derivedFrom":makeQuery(id+"F17.opExtrude","SWEPT_EDGE",EDGE,{"disambiguationData":[OSD([sQuery(id+"F16.wireOp",EDGE,"E42"),sQuery(id+"F16.wireOp",EDGE,"E43")])]})});
            var Q8;
            Q8=makeQuery(id+"F17.boolean.opBoolean","COPY",EDGE,{"derivedFrom":makeQuery(id+"F17.opExtrude","SWEPT_EDGE",EDGE,{"disambiguationData":[OSD([sQuery(id+"F16.wireOp",EDGE,"E43"),sQuery(id+"F16.wireOp",EDGE,"E44")])]})});
            fillet(context, id + "F19", {"entities" : qUnion([Q0, Q1, Q2, Q3, Q4, Q5, Q6, Q7, Q8]), "radius" : 0.2 * mm, "tangentPropagation" : true, "allowEdgeOverflow" : false});
        }
    });